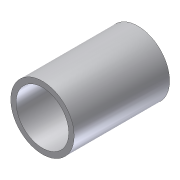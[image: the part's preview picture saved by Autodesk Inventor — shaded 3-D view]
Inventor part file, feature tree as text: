
AUTODESK INVENTOR PART (.ipt)
format: ipt  version: 2012 (Build 160160000, 160)  size: 79,872 bytes
history: native  units: in
note: dims shown in document units (in); Inventor stores cm internally (conversion verified against a paired STEP export)
features: extrude x1, shell x1, sketch x1
ambient origin geometry x8: Origin, YZ Plane, XZ Plane, XY Plane, X Axis, Y Axis, Z Axis, Center Point
bodies: Solid1 (feature_tree)
feature tree (3):
  extrude  "Extrusion1"  Depth=2.5in TaperAngle=0.0deg
  shell  "Shell1"  Thickness=0.14in
  sketch  "Sketch1"  dims[d0=1.66in d1=2.5in d2=0.0in d3=0.14in]
